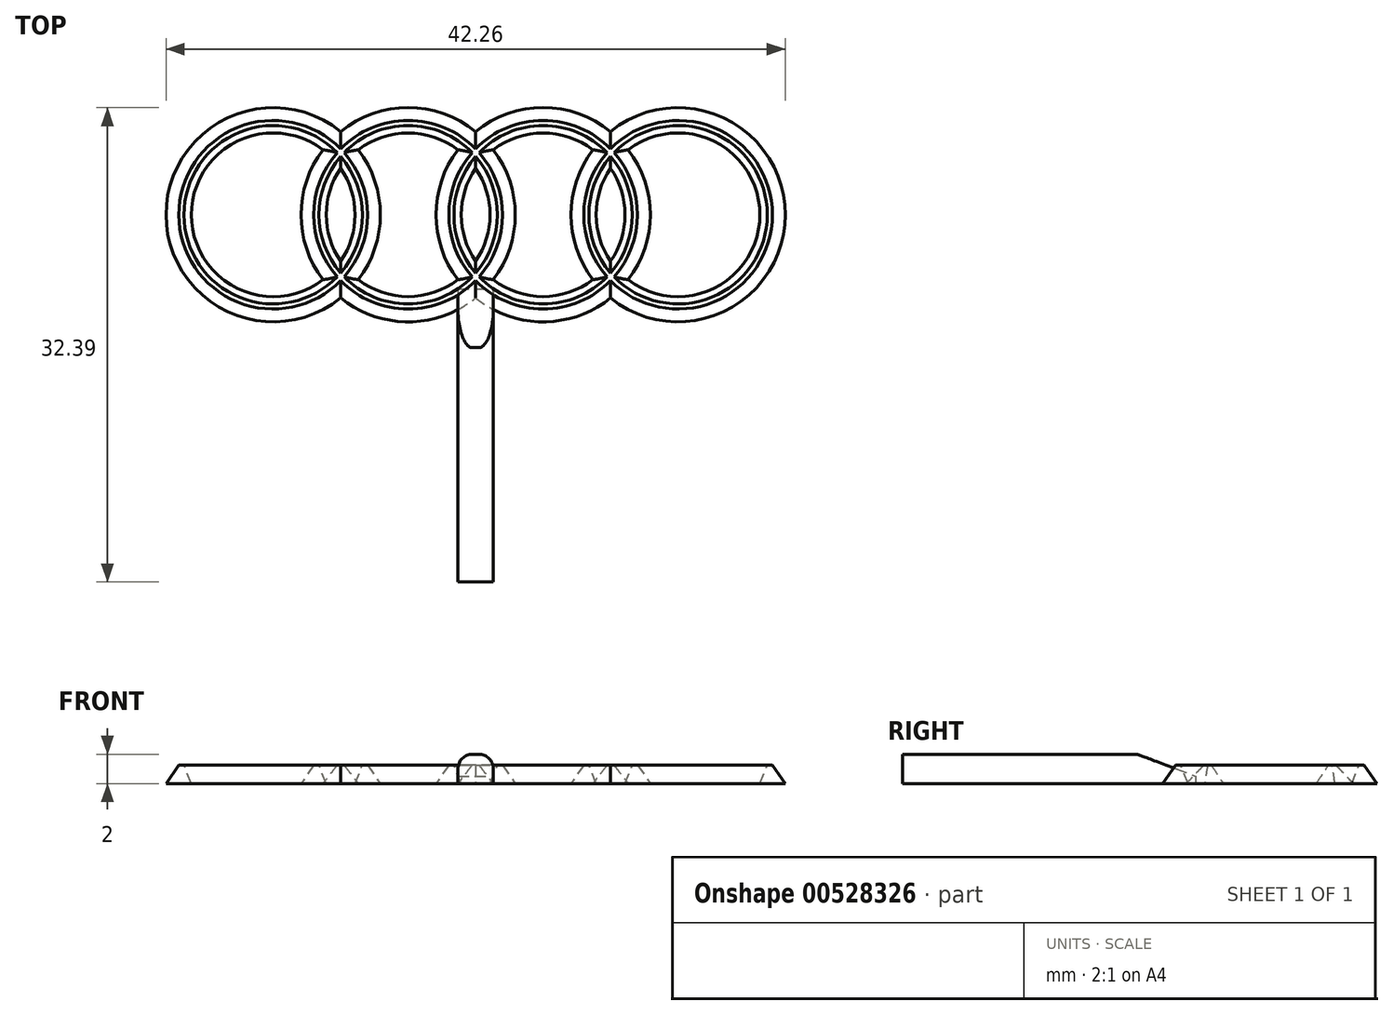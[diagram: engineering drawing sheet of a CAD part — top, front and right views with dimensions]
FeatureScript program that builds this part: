
annotation { "Feature Type Name" : "Feature", "Feature Type Description" : "" }
export const myFeature = defineFeature(function(context is Context, id is Id, definition is map)
    precondition{}
    {
        {
            var Q0;
            Q0=qCreatedBy(makeId("Top.planeOp"),FACE);
            var sketch = newSketch(context, id + "F0", { "sketchPlane" : qUnion([Q0])});
            skLineSegment(sketch, "E0", {"start": v(-55.28, 29.34) * mm, "end": v(-55.28, -29.34) * mm, "construction": true});
            skLineSegment(sketch, "E1", {"start": v(-55.28, -29.34) * mm, "end": v(55.28, -29.34) * mm, "construction": true});
            skLineSegment(sketch, "E2", {"start": v(55.27, -29.34) * mm, "end": v(55.27, 29.34) * mm, "construction": true});
            skLineSegment(sketch, "E3", {"start": v(55.28, 29.34) * mm, "end": v(-67.88, 29.34) * mm, "construction": true});
            skLineSegment(sketch, "E4", {"start": v(-55.28, 0) * mm, "end": v(55.28, 0) * mm, "construction": true});
            skPoint(sketch, "E5", {"position": v(0, 0) * mm});
            skLineSegment(sketch, "E6", {"start": v(-18.43, 29.34) * mm, "end": v(-18.43, -29.34) * mm, "construction": true});
            skLineSegment(sketch, "E7", {"start": v(18.42, -29.34) * mm, "end": v(18.42, 29.34) * mm, "construction": true});
            skCircle(sketch, "E8", {"center": v(-55.28, 0) * mm, "radius": 22.35 * mm});
            skCircle(sketch, "E9", {"center": v(-55.28, 0) * mm, "radius": 29.25 * mm});
            skCircle(sketch, "E10", {"center": v(-18.43, 0) * mm, "radius": 22.35 * mm});
            skCircle(sketch, "E11", {"center": v(-18.43, 0) * mm, "radius": 29.25 * mm});
            skCircle(sketch, "E12", {"center": v(18.42, 0) * mm, "radius": 22.35 * mm});
            skCircle(sketch, "E13", {"center": v(18.42, 0) * mm, "radius": 29.25 * mm});
            skCircle(sketch, "E14", {"center": v(55.28, 0) * mm, "radius": 22.35 * mm});
            skCircle(sketch, "E15", {"center": v(55.28, 0) * mm, "radius": 29.25 * mm});
            skSolve(sketch);
        }
        {
            var Q0;
            {var subQ0=sQuery(id+"F0.wireOp",EDGE,"E12");var subQ1=sQuery(id+"F0.wireOp",EDGE,"E10");var subQ2=makeQuery(id+"F0.imprint","INTERSECT",VERTEX,{"disambiguationData":[OD(0.0)],"derivedFrom":[subQ1,subQ0]});Q0=makeQuery(id+"F0.imprint","IMPRINT",FACE,{"disambiguationData":[TD([[makeQuery(id+"F0.imprint","IMPRINT",EDGE,{"disambiguationData":[TD([[subQ2,1.0]])],"derivedFrom":subQ1}),-1.0]])]});}
            var Q1;
            {var subQ0=sQuery(id+"F0.wireOp",EDGE,"E13");var subQ1=sQuery(id+"F0.wireOp",EDGE,"E10");var subQ2=makeQuery(id+"F0.imprint","INTERSECT",VERTEX,{"disambiguationData":[OD(0.0)],"derivedFrom":[subQ1,subQ0]});Q1=makeQuery(id+"F0.imprint","IMPRINT",FACE,{"disambiguationData":[TD([[makeQuery(id+"F0.imprint","IMPRINT",EDGE,{"disambiguationData":[TD([[subQ2,1.0]])],"derivedFrom":subQ1}),-1.0]])]});}
            var Q2;
            {var subQ0=sQuery(id+"F0.wireOp",EDGE,"E14");var subQ1=sQuery(id+"F0.wireOp",EDGE,"E12");var subQ2=makeQuery(id+"F0.imprint","INTERSECT",VERTEX,{"disambiguationData":[OD(0.0)],"derivedFrom":[subQ1,subQ0]});Q2=makeQuery(id+"F0.imprint","IMPRINT",FACE,{"disambiguationData":[TD([[makeQuery(id+"F0.imprint","IMPRINT",EDGE,{"disambiguationData":[TD([[subQ2,1.0]])],"derivedFrom":subQ1}),-1.0]])]});}
            var Q3;
            {var subQ0=sQuery(id+"F0.wireOp",EDGE,"E15");var subQ1=sQuery(id+"F0.wireOp",EDGE,"E12");var subQ2=makeQuery(id+"F0.imprint","INTERSECT",VERTEX,{"disambiguationData":[OD(0.0)],"derivedFrom":[subQ1,subQ0]});Q3=makeQuery(id+"F0.imprint","IMPRINT",FACE,{"disambiguationData":[TD([[makeQuery(id+"F0.imprint","IMPRINT",EDGE,{"disambiguationData":[TD([[subQ2,1.0]])],"derivedFrom":subQ1}),-1.0]])]});}
            var Q4;
            {var subQ0=sQuery(id+"F0.wireOp",EDGE,"E13");var subQ1=sQuery(id+"F0.wireOp",EDGE,"E10");var subQ2=makeQuery(id+"F0.imprint","INTERSECT",VERTEX,{"disambiguationData":[OD(1.0)],"derivedFrom":[subQ1,subQ0]});Q4=makeQuery(id+"F0.imprint","IMPRINT",FACE,{"disambiguationData":[TD([[makeQuery(id+"F0.imprint","IMPRINT",EDGE,{"disambiguationData":[TD([[subQ2,-1.0]])],"derivedFrom":subQ1}),-1.0]])]});}
            var Q5;
            {var subQ0=sQuery(id+"F0.wireOp",EDGE,"E11");var subQ1=sQuery(id+"F0.wireOp",EDGE,"E8");var subQ2=makeQuery(id+"F0.imprint","INTERSECT",VERTEX,{"disambiguationData":[OD(1.0)],"derivedFrom":[subQ1,subQ0]});Q5=makeQuery(id+"F0.imprint","IMPRINT",FACE,{"disambiguationData":[TD([[makeQuery(id+"F0.imprint","IMPRINT",EDGE,{"disambiguationData":[TD([[subQ2,-1.0]])],"derivedFrom":subQ1}),-1.0]])]});}
            var Q6;
            {var subQ0=sQuery(id+"F0.wireOp",EDGE,"E10");var subQ1=sQuery(id+"F0.wireOp",EDGE,"E8");var subQ2=makeQuery(id+"F0.imprint","INTERSECT",VERTEX,{"disambiguationData":[OD(0.0)],"derivedFrom":[subQ1,subQ0]});Q6=makeQuery(id+"F0.imprint","IMPRINT",FACE,{"disambiguationData":[TD([[makeQuery(id+"F0.imprint","IMPRINT",EDGE,{"disambiguationData":[TD([[subQ2,1.0]])],"derivedFrom":subQ1}),-1.0]])]});}
            var Q7;
            {var subQ0=sQuery(id+"F0.wireOp",EDGE,"E13");var subQ1=sQuery(id+"F0.wireOp",EDGE,"E10");var subQ2=makeQuery(id+"F0.imprint","INTERSECT",VERTEX,{"disambiguationData":[OD(0.0)],"derivedFrom":[subQ1,subQ0]});Q7=makeQuery(id+"F0.imprint","IMPRINT",FACE,{"disambiguationData":[TD([[makeQuery(id+"F0.imprint","IMPRINT",EDGE,{"disambiguationData":[TD([[subQ2,1.0]])],"derivedFrom":subQ1}),1.0]])]});}
            var Q8;
            {var subQ0=sQuery(id+"F0.wireOp",EDGE,"E11");var subQ1=sQuery(id+"F0.wireOp",EDGE,"E8");var subQ2=makeQuery(id+"F0.imprint","INTERSECT",VERTEX,{"disambiguationData":[OD(0.0)],"derivedFrom":[subQ1,subQ0]});Q8=makeQuery(id+"F0.imprint","IMPRINT",FACE,{"disambiguationData":[TD([[makeQuery(id+"F0.imprint","IMPRINT",EDGE,{"disambiguationData":[TD([[subQ2,-1.0]])],"derivedFrom":subQ1}),-1.0]])]});}
            var Q9;
            {var subQ0=sQuery(id+"F0.wireOp",EDGE,"E11");var subQ1=sQuery(id+"F0.wireOp",EDGE,"E9");var subQ2=makeQuery(id+"F0.imprint","INTERSECT",VERTEX,{"disambiguationData":[OD(0.0)],"derivedFrom":[subQ1,subQ0]});Q9=makeQuery(id+"F0.imprint","IMPRINT",FACE,{"disambiguationData":[TD([[makeQuery(id+"F0.imprint","IMPRINT",EDGE,{"disambiguationData":[TD([[subQ2,1.0]])],"derivedFrom":subQ1}),-1.0]])]});}
            var Q10;
            {var subQ0=sQuery(id+"F0.wireOp",EDGE,"E11");var subQ1=sQuery(id+"F0.wireOp",EDGE,"E9");var subQ2=makeQuery(id+"F0.imprint","INTERSECT",VERTEX,{"disambiguationData":[OD(1.0)],"derivedFrom":[subQ1,subQ0]});Q10=makeQuery(id+"F0.imprint","IMPRINT",FACE,{"disambiguationData":[TD([[makeQuery(id+"F0.imprint","IMPRINT",EDGE,{"disambiguationData":[TD([[subQ2,-1.0]])],"derivedFrom":subQ1}),-1.0]])]});}
            var Q11;
            {var subQ0=sQuery(id+"F0.wireOp",EDGE,"E13");var subQ1=sQuery(id+"F0.wireOp",EDGE,"E11");var subQ2=makeQuery(id+"F0.imprint","INTERSECT",VERTEX,{"disambiguationData":[OD(0.0)],"derivedFrom":[subQ1,subQ0]});Q11=makeQuery(id+"F0.imprint","IMPRINT",FACE,{"disambiguationData":[TD([[makeQuery(id+"F0.imprint","IMPRINT",EDGE,{"disambiguationData":[TD([[subQ2,1.0]])],"derivedFrom":subQ1}),-1.0]])]});}
            var Q12;
            {var subQ0=sQuery(id+"F0.wireOp",EDGE,"E13");var subQ1=sQuery(id+"F0.wireOp",EDGE,"E11");var subQ2=makeQuery(id+"F0.imprint","INTERSECT",VERTEX,{"disambiguationData":[OD(1.0)],"derivedFrom":[subQ1,subQ0]});Q12=makeQuery(id+"F0.imprint","IMPRINT",FACE,{"disambiguationData":[TD([[makeQuery(id+"F0.imprint","IMPRINT",EDGE,{"disambiguationData":[TD([[subQ2,-1.0]])],"derivedFrom":subQ1}),-1.0]])]});}
            var Q13;
            {var subQ0=sQuery(id+"F0.wireOp",EDGE,"E15");var subQ1=sQuery(id+"F0.wireOp",EDGE,"E13");var subQ2=makeQuery(id+"F0.imprint","INTERSECT",VERTEX,{"disambiguationData":[OD(0.0)],"derivedFrom":[subQ1,subQ0]});Q13=makeQuery(id+"F0.imprint","IMPRINT",FACE,{"disambiguationData":[TD([[makeQuery(id+"F0.imprint","IMPRINT",EDGE,{"disambiguationData":[TD([[subQ2,1.0]])],"derivedFrom":subQ1}),-1.0]])]});}
            var Q14;
            {var subQ0=sQuery(id+"F0.wireOp",EDGE,"E11");var subQ1=sQuery(id+"F0.wireOp",EDGE,"E8");var subQ2=makeQuery(id+"F0.imprint","INTERSECT",VERTEX,{"disambiguationData":[OD(0.0)],"derivedFrom":[subQ1,subQ0]});Q14=makeQuery(id+"F0.imprint","IMPRINT",FACE,{"disambiguationData":[TD([[makeQuery(id+"F0.imprint","IMPRINT",EDGE,{"disambiguationData":[TD([[subQ2,1.0]])],"derivedFrom":subQ1}),1.0]])]});}
            var Q15;
            {var subQ0=sQuery(id+"F0.wireOp",EDGE,"E11");var subQ1=sQuery(id+"F0.wireOp",EDGE,"E8");var subQ2=makeQuery(id+"F0.imprint","INTERSECT",VERTEX,{"disambiguationData":[OD(0.0)],"derivedFrom":[subQ1,subQ0]});Q15=makeQuery(id+"F0.imprint","IMPRINT",FACE,{"disambiguationData":[TD([[makeQuery(id+"F0.imprint","IMPRINT",EDGE,{"disambiguationData":[TD([[subQ2,1.0]])],"derivedFrom":subQ1}),-1.0]])]});}
            var Q16;
            {var subQ0=sQuery(id+"F0.wireOp",EDGE,"E15");var subQ1=sQuery(id+"F0.wireOp",EDGE,"E12");var subQ2=makeQuery(id+"F0.imprint","INTERSECT",VERTEX,{"disambiguationData":[OD(1.0)],"derivedFrom":[subQ1,subQ0]});Q16=makeQuery(id+"F0.imprint","IMPRINT",FACE,{"disambiguationData":[TD([[makeQuery(id+"F0.imprint","IMPRINT",EDGE,{"disambiguationData":[TD([[subQ2,-1.0]])],"derivedFrom":subQ1}),-1.0]])]});}
            var Q17;
            {var subQ0=sQuery(id+"F0.wireOp",EDGE,"E15");var subQ1=sQuery(id+"F0.wireOp",EDGE,"E12");var subQ2=makeQuery(id+"F0.imprint","INTERSECT",VERTEX,{"disambiguationData":[OD(0.0)],"derivedFrom":[subQ1,subQ0]});Q17=makeQuery(id+"F0.imprint","IMPRINT",FACE,{"disambiguationData":[TD([[makeQuery(id+"F0.imprint","IMPRINT",EDGE,{"disambiguationData":[TD([[subQ2,1.0]])],"derivedFrom":subQ1}),1.0]])]});}
            extrude(context, id + "F1", {"entities" : qUnion([Q0, Q1, Q2, Q3, Q4, Q5, Q6, Q7, Q8, Q9, Q10, Q11, Q12, Q13, Q14, Q15, Q16, Q17]), "depth" : 5 * mm});
        }
        {
            var Q0;
            {var subQ0=sQuery(id+"F0.wireOp",EDGE,"E11");var subQ1=sQuery(id+"F0.wireOp",EDGE,"E9");Q0=makeQuery(id+"F1.opExtrude","CAP_EDGE",EDGE,{"disambiguationData":[OSD([subQ1]),TDD([makeQuery(id+"F0.imprint","IMPRINT",EDGE,{"disambiguationData":[TD([[makeQuery(id+"F0.imprint","INTERSECT",VERTEX,{"disambiguationData":[OD(0.0)],"derivedFrom":[subQ1,subQ0]}),-1.0]])],"derivedFrom":subQ1})])],"isStart":false});}
            var Q1;
            {var subQ0=sQuery(id+"F0.wireOp",EDGE,"E11");Q1=makeQuery(id+"F1.opExtrude","CAP_EDGE",EDGE,{"disambiguationData":[OSD([subQ0]),TDD([makeQuery(id+"F0.imprint","IMPRINT",EDGE,{"disambiguationData":[TD([[makeQuery(id+"F0.imprint","INTERSECT",VERTEX,{"disambiguationData":[OD(0.0)],"derivedFrom":[sQuery(id+"F0.wireOp",EDGE,"E9"),subQ0]}),1.0]])],"derivedFrom":subQ0})])],"isStart":false});}
            var Q2;
            {var subQ0=sQuery(id+"F0.wireOp",EDGE,"E13");Q2=makeQuery(id+"F1.opExtrude","CAP_EDGE",EDGE,{"disambiguationData":[OSD([subQ0]),TDD([makeQuery(id+"F0.imprint","IMPRINT",EDGE,{"disambiguationData":[TD([[makeQuery(id+"F0.imprint","INTERSECT",VERTEX,{"disambiguationData":[OD(0.0)],"derivedFrom":[sQuery(id+"F0.wireOp",EDGE,"E11"),subQ0]}),1.0]])],"derivedFrom":subQ0})])],"isStart":false});}
            var Q3;
            {var subQ0=sQuery(id+"F0.wireOp",EDGE,"E15");var subQ1=sQuery(id+"F0.wireOp",EDGE,"E13");Q3=makeQuery(id+"F1.opExtrude","CAP_EDGE",EDGE,{"disambiguationData":[OSD([subQ0]),TDD([makeQuery(id+"F0.imprint","IMPRINT",EDGE,{"disambiguationData":[TD([[makeQuery(id+"F0.imprint","INTERSECT",VERTEX,{"disambiguationData":[OD(0.0)],"derivedFrom":[subQ1,subQ0]}),1.0]])],"derivedFrom":subQ0})])],"isStart":false});}
            var Q4;
            {var subQ0=sQuery(id+"F0.wireOp",EDGE,"E13");Q4=makeQuery(id+"F1.opExtrude","CAP_EDGE",EDGE,{"disambiguationData":[OSD([subQ0]),TDD([makeQuery(id+"F0.imprint","IMPRINT",EDGE,{"disambiguationData":[TD([[makeQuery(id+"F0.imprint","INTERSECT",VERTEX,{"disambiguationData":[OD(1.0)],"derivedFrom":[sQuery(id+"F0.wireOp",EDGE,"E11"),subQ0]}),-1.0]])],"derivedFrom":subQ0})])],"isStart":false});}
            var Q5;
            {var subQ0=sQuery(id+"F0.wireOp",EDGE,"E11");Q5=makeQuery(id+"F1.opExtrude","CAP_EDGE",EDGE,{"disambiguationData":[OSD([subQ0]),TDD([makeQuery(id+"F0.imprint","IMPRINT",EDGE,{"disambiguationData":[TD([[makeQuery(id+"F0.imprint","INTERSECT",VERTEX,{"disambiguationData":[OD(1.0)],"derivedFrom":[sQuery(id+"F0.wireOp",EDGE,"E9"),subQ0]}),-1.0]])],"derivedFrom":subQ0})])],"isStart":false});}
            var Q6;
            {var subQ0=sQuery(id+"F0.wireOp",EDGE,"E10");var subQ1=sQuery(id+"F0.wireOp",EDGE,"E9");Q6=makeQuery(id+"F1.opExtrude","CAP_EDGE",EDGE,{"disambiguationData":[OSD([subQ1]),TDD([makeQuery(id+"F0.imprint","IMPRINT",EDGE,{"disambiguationData":[TD([[makeQuery(id+"F0.imprint","INTERSECT",VERTEX,{"disambiguationData":[OD(0.0)],"derivedFrom":[subQ1,subQ0]}),1.0]])],"derivedFrom":subQ1})])],"isStart":false});}
            var Q7;
            {var subQ0=sQuery(id+"F0.wireOp",EDGE,"E11");var subQ1=sQuery(id+"F0.wireOp",EDGE,"E8");Q7=makeQuery(id+"F1.opExtrude","CAP_EDGE",EDGE,{"disambiguationData":[OSD([subQ0]),TDD([makeQuery(id+"F0.imprint","IMPRINT",EDGE,{"disambiguationData":[TD([[makeQuery(id+"F0.imprint","INTERSECT",VERTEX,{"disambiguationData":[OD(0.0)],"derivedFrom":[subQ1,subQ0]}),-1.0]])],"derivedFrom":subQ0})])],"isStart":false});}
            var Q8;
            {var subQ0=sQuery(id+"F0.wireOp",EDGE,"E13");var subQ1=sQuery(id+"F0.wireOp",EDGE,"E10");Q8=makeQuery(id+"F1.opExtrude","CAP_EDGE",EDGE,{"disambiguationData":[OSD([subQ0]),TDD([makeQuery(id+"F0.imprint","IMPRINT",EDGE,{"disambiguationData":[TD([[makeQuery(id+"F0.imprint","INTERSECT",VERTEX,{"disambiguationData":[OD(0.0)],"derivedFrom":[subQ1,subQ0]}),-1.0]])],"derivedFrom":subQ0})])],"isStart":false});}
            var Q9;
            {var subQ0=sQuery(id+"F0.wireOp",EDGE,"E12");var subQ1=sQuery(id+"F0.wireOp",EDGE,"E11");Q9=makeQuery(id+"F1.opExtrude","CAP_EDGE",EDGE,{"disambiguationData":[OSD([subQ1]),TDD([makeQuery(id+"F0.imprint","IMPRINT",EDGE,{"disambiguationData":[TD([[makeQuery(id+"F0.imprint","INTERSECT",VERTEX,{"disambiguationData":[OD(0.0)],"derivedFrom":[subQ1,subQ0]}),1.0]])],"derivedFrom":subQ1})])],"isStart":false});}
            var Q10;
            {var subQ0=sQuery(id+"F0.wireOp",EDGE,"E15");var subQ1=sQuery(id+"F0.wireOp",EDGE,"E12");Q10=makeQuery(id+"F1.opExtrude","CAP_EDGE",EDGE,{"disambiguationData":[OSD([subQ0]),TDD([makeQuery(id+"F0.imprint","IMPRINT",EDGE,{"disambiguationData":[TD([[makeQuery(id+"F0.imprint","INTERSECT",VERTEX,{"disambiguationData":[OD(0.0)],"derivedFrom":[subQ1,subQ0]}),-1.0]])],"derivedFrom":subQ0})])],"isStart":false});}
            var Q11;
            {var subQ0=sQuery(id+"F0.wireOp",EDGE,"E14");var subQ1=sQuery(id+"F0.wireOp",EDGE,"E13");Q11=makeQuery(id+"F1.opExtrude","CAP_EDGE",EDGE,{"disambiguationData":[OSD([subQ1]),TDD([makeQuery(id+"F0.imprint","IMPRINT",EDGE,{"disambiguationData":[TD([[makeQuery(id+"F0.imprint","INTERSECT",VERTEX,{"disambiguationData":[OD(0.0)],"derivedFrom":[subQ1,subQ0]}),1.0]])],"derivedFrom":subQ1})])],"isStart":false});}
            chamfer(context, id + "F2", {"entities" : qUnion([Q0, Q1, Q2, Q3, Q4, Q5, Q6, Q7, Q8, Q9, Q10, Q11]), "chamferType" : ChamferType.TWO_OFFSETS, "width1" : 5 * mm, "oppositeDirection" : true, "width2" : 3.5 * mm, "tangentPropagation" : true});
        }
        {
            var Q0;
            {var subQ0=sQuery(id+"F0.wireOp",EDGE,"E11");var subQ1=sQuery(id+"F0.wireOp",EDGE,"E8");Q0=makeQuery(id+"F1.opExtrude","CAP_EDGE",EDGE,{"disambiguationData":[OSD([subQ1]),TDD([makeQuery(id+"F0.imprint","IMPRINT",EDGE,{"disambiguationData":[TD([[makeQuery(id+"F0.imprint","INTERSECT",VERTEX,{"disambiguationData":[OD(0.0)],"derivedFrom":[subQ1,subQ0]}),-1.0]])],"derivedFrom":subQ1})])],"isStart":false});}
            var Q1;
            {var subQ0=sQuery(id+"F0.wireOp",EDGE,"E10");var subQ1=sQuery(id+"F0.wireOp",EDGE,"E8");Q1=makeQuery(id+"F1.opExtrude","CAP_EDGE",EDGE,{"disambiguationData":[OSD([subQ0]),TDD([makeQuery(id+"F0.imprint","IMPRINT",EDGE,{"disambiguationData":[TD([[makeQuery(id+"F0.imprint","INTERSECT",VERTEX,{"disambiguationData":[OD(0.0)],"derivedFrom":[subQ1,subQ0]}),-1.0]])],"derivedFrom":subQ0})])],"isStart":false});}
            var Q2;
            {var subQ0=sQuery(id+"F0.wireOp",EDGE,"E10");var subQ1=sQuery(id+"F0.wireOp",EDGE,"E8");Q2=makeQuery(id+"F1.opExtrude","CAP_EDGE",EDGE,{"disambiguationData":[OSD([subQ1]),TDD([makeQuery(id+"F0.imprint","IMPRINT",EDGE,{"disambiguationData":[TD([[makeQuery(id+"F0.imprint","INTERSECT",VERTEX,{"disambiguationData":[OD(0.0)],"derivedFrom":[subQ1,subQ0]}),1.0]])],"derivedFrom":subQ1})])],"isStart":false});}
            var Q3;
            {var subQ0=sQuery(id+"F0.wireOp",EDGE,"E12");var subQ1=sQuery(id+"F0.wireOp",EDGE,"E10");Q3=makeQuery(id+"F1.opExtrude","CAP_EDGE",EDGE,{"disambiguationData":[OSD([subQ0]),TDD([makeQuery(id+"F0.imprint","IMPRINT",EDGE,{"disambiguationData":[TD([[makeQuery(id+"F0.imprint","INTERSECT",VERTEX,{"disambiguationData":[OD(0.0)],"derivedFrom":[subQ1,subQ0]}),-1.0]])],"derivedFrom":subQ0})])],"isStart":false});}
            var Q4;
            {var subQ0=sQuery(id+"F0.wireOp",EDGE,"E12");var subQ1=sQuery(id+"F0.wireOp",EDGE,"E10");Q4=makeQuery(id+"F1.opExtrude","CAP_EDGE",EDGE,{"disambiguationData":[OSD([subQ1]),TDD([makeQuery(id+"F0.imprint","IMPRINT",EDGE,{"disambiguationData":[TD([[makeQuery(id+"F0.imprint","INTERSECT",VERTEX,{"disambiguationData":[OD(0.0)],"derivedFrom":[subQ1,subQ0]}),1.0]])],"derivedFrom":subQ1})])],"isStart":false});}
            var Q5;
            {var subQ0=sQuery(id+"F0.wireOp",EDGE,"E14");var subQ1=sQuery(id+"F0.wireOp",EDGE,"E12");Q5=makeQuery(id+"F1.opExtrude","CAP_EDGE",EDGE,{"disambiguationData":[OSD([subQ0]),TDD([makeQuery(id+"F0.imprint","IMPRINT",EDGE,{"disambiguationData":[TD([[makeQuery(id+"F0.imprint","INTERSECT",VERTEX,{"disambiguationData":[OD(0.0)],"derivedFrom":[subQ1,subQ0]}),-1.0]])],"derivedFrom":subQ0})])],"isStart":false});}
            var Q6;
            {var subQ0=sQuery(id+"F0.wireOp",EDGE,"E14");var subQ1=sQuery(id+"F0.wireOp",EDGE,"E12");Q6=makeQuery(id+"F1.opExtrude","CAP_EDGE",EDGE,{"disambiguationData":[OSD([subQ1]),TDD([makeQuery(id+"F0.imprint","IMPRINT",EDGE,{"disambiguationData":[TD([[makeQuery(id+"F0.imprint","INTERSECT",VERTEX,{"disambiguationData":[OD(0.0)],"derivedFrom":[subQ1,subQ0]}),1.0]])],"derivedFrom":subQ1})])],"isStart":false});}
            var Q7;
            {var subQ0=sQuery(id+"F0.wireOp",EDGE,"E12");Q7=makeQuery(id+"F1.opExtrude","CAP_EDGE",EDGE,{"disambiguationData":[OSD([subQ0]),TDD([makeQuery(id+"F0.imprint","IMPRINT",EDGE,{"disambiguationData":[TD([[makeQuery(id+"F0.imprint","INTERSECT",VERTEX,{"disambiguationData":[OD(0.0)],"derivedFrom":[sQuery(id+"F0.wireOp",EDGE,"E11"),subQ0]}),1.0]])],"derivedFrom":subQ0})])],"isStart":false});}
            var Q8;
            {var subQ0=sQuery(id+"F0.wireOp",EDGE,"E10");Q8=makeQuery(id+"F1.opExtrude","CAP_EDGE",EDGE,{"disambiguationData":[OSD([subQ0]),TDD([makeQuery(id+"F0.imprint","IMPRINT",EDGE,{"disambiguationData":[TD([[makeQuery(id+"F0.imprint","INTERSECT",VERTEX,{"disambiguationData":[OD(0.0)],"derivedFrom":[sQuery(id+"F0.wireOp",EDGE,"E9"),subQ0]}),1.0]])],"derivedFrom":subQ0})])],"isStart":false});}
            var Q9;
            {var subQ0=sQuery(id+"F0.wireOp",EDGE,"E10");Q9=makeQuery(id+"F1.opExtrude","CAP_EDGE",EDGE,{"disambiguationData":[OSD([subQ0]),TDD([makeQuery(id+"F0.imprint","IMPRINT",EDGE,{"disambiguationData":[TD([[makeQuery(id+"F0.imprint","INTERSECT",VERTEX,{"disambiguationData":[OD(1.0)],"derivedFrom":[sQuery(id+"F0.wireOp",EDGE,"E9"),subQ0]}),-1.0]])],"derivedFrom":subQ0})])],"isStart":false});}
            var Q10;
            {var subQ0=sQuery(id+"F0.wireOp",EDGE,"E12");Q10=makeQuery(id+"F1.opExtrude","CAP_EDGE",EDGE,{"disambiguationData":[OSD([subQ0]),TDD([makeQuery(id+"F0.imprint","IMPRINT",EDGE,{"disambiguationData":[TD([[makeQuery(id+"F0.imprint","INTERSECT",VERTEX,{"disambiguationData":[OD(1.0)],"derivedFrom":[sQuery(id+"F0.wireOp",EDGE,"E11"),subQ0]}),-1.0]])],"derivedFrom":subQ0})])],"isStart":false});}
            var Q11;
            {var subQ0=sQuery(id+"F0.wireOp",EDGE,"E14");var subQ1=sQuery(id+"F0.wireOp",EDGE,"E13");Q11=makeQuery(id+"F1.opExtrude","CAP_EDGE",EDGE,{"disambiguationData":[OSD([subQ0]),TDD([makeQuery(id+"F0.imprint","IMPRINT",EDGE,{"disambiguationData":[TD([[makeQuery(id+"F0.imprint","INTERSECT",VERTEX,{"disambiguationData":[OD(0.0)],"derivedFrom":[subQ1,subQ0]}),1.0]])],"derivedFrom":subQ0})])],"isStart":false});}
            chamfer(context, id + "F3", {"entities" : qUnion([Q0, Q1, Q2, Q3, Q4, Q5, Q6, Q7, Q8, Q9, Q10, Q11]), "chamferType" : ChamferType.TWO_OFFSETS, "width1" : 5 * mm, "oppositeDirection" : false, "width2" : 2 * mm, "tangentPropagation" : true});
        }
        {
            var Q0;
            Q0=makeQuery(id+"F1.opExtrude","SWEPT_BODY",BODY,{"disambiguationData":[OSD([sQuery(id+"F0.wireOp",EDGE,"E8"),sQuery(id+"F0.wireOp",EDGE,"E9"),sQuery(id+"F0.wireOp",EDGE,"E10"),sQuery(id+"F0.wireOp",EDGE,"E11"),sQuery(id+"F0.wireOp",EDGE,"E12"),sQuery(id+"F0.wireOp",EDGE,"E13"),sQuery(id+"F0.wireOp",EDGE,"E14"),sQuery(id+"F0.wireOp",EDGE,"E15")])]});
            var Q1;
            Q1=qCreatedBy(makeId("Origin.pointOp"),VERTEX);
            transform(context, id + "F4", {"entities" : qUnion([Q0]), "transformType" : TransformType.SCALE_UNIFORMLY, "scale" : 0.25, "scalePoint" : qUnion([Q1]), "makeCopy" : false});
        }
        {
            var Q0;
            Q0=qCreatedBy(makeId("Top.planeOp"),FACE);
            var sketch = newSketch(context, id + "F5", { "sketchPlane" : qUnion([Q0])});
            skArc(sketch, "E16.0", {"start": v(-9.21, 5.68) * mm, "mid": v(-21.13, 0) * mm, "end": v(-9.21, -5.68) * mm, "construction": true});
            skArc(sketch, "E17.0", {"start": v(9.21, -5.68) * mm, "mid": v(21.13, 0) * mm, "end": v(9.21, 5.68) * mm, "construction": true});
            skArc(sketch, "E18.0", {"start": v(0, -5.68) * mm, "mid": v(4.6, -7.31) * mm, "end": v(9.21, -5.68) * mm, "construction": true});
            skArc(sketch, "E19.0", {"start": v(-9.21, -5.68) * mm, "mid": v(-4.6, -7.31) * mm, "end": v(0, -5.68) * mm, "construction": true});
            skArc(sketch, "E20.0", {"start": v(0, 5.68) * mm, "mid": v(-4.6, 7.31) * mm, "end": v(-9.21, 5.68) * mm, "construction": true});
            skArc(sketch, "E21.0", {"start": v(9.21, 5.68) * mm, "mid": v(4.6, 7.31) * mm, "end": v(0, 5.68) * mm, "construction": true});
            skLineSegment(sketch, "E22", {"start": v(-21.13, 0) * mm, "end": v(21.13, 0) * mm, "construction": true});
            skPoint(sketch, "E22.startSnap0", {"position": v(-21.13, 0) * mm});
            skLineSegment(sketch, "E23.bottom", {"start": v(-51.13, 0.8) * mm, "end": v(-21.13, 0.8) * mm});
            skLineSegment(sketch, "E23.top", {"start": v(-51.13, -0.8) * mm, "end": v(-21.13, -0.8) * mm});
            skLineSegment(sketch, "E23.left", {"start": v(-51.13, 0.8) * mm, "end": v(-51.13, -0.8) * mm});
            skLineSegment(sketch, "E23.right", {"start": v(-21.13, 0.8) * mm, "end": v(-21.13, -0.8) * mm});
            skPoint(sketch, "E24.orphan", {"position": v(-32.97, 0) * mm});
            skLineSegment(sketch, "E25.bottom", {"start": v(21.13, -0.8) * mm, "end": v(51.13, -0.8) * mm});
            skLineSegment(sketch, "E25.top", {"start": v(21.13, 0.8) * mm, "end": v(51.13, 0.8) * mm});
            skLineSegment(sketch, "E25.left", {"start": v(21.13, -0.8) * mm, "end": v(21.13, 0.8) * mm});
            skLineSegment(sketch, "E25.right", {"start": v(51.13, -0.8) * mm, "end": v(51.13, 0.8) * mm});
            skPoint(sketch, "E26", {"position": v(21.13, 0) * mm});
            skLineSegment(sketch, "E27", {"start": v(-23.13, -0.8) * mm, "end": v(-23.13, 0.8) * mm});
            skLineSegment(sketch, "E28", {"start": v(23.13, -0.8) * mm, "end": v(23.13, 0.8) * mm});
            skLineSegment(sketch, "E29.bottom", {"start": v(-21.13, -0.8) * mm, "end": v(-20.13, -0.8) * mm});
            skLineSegment(sketch, "E29.top", {"start": v(-21.13, 0.8) * mm, "end": v(-20.13, 0.8) * mm});
            skLineSegment(sketch, "E29.left", {"start": v(-21.13, -0.8) * mm, "end": v(-21.13, 0.8) * mm});
            skLineSegment(sketch, "E29.right", {"start": v(-20.13, -0.8) * mm, "end": v(-20.13, 0.8) * mm});
            skLineSegment(sketch, "E30.bottom", {"start": v(21.13, -0.8) * mm, "end": v(20.13, -0.8) * mm});
            skLineSegment(sketch, "E30.top", {"start": v(21.13, 0.8) * mm, "end": v(20.13, 0.8) * mm});
            skLineSegment(sketch, "E30.right", {"start": v(20.13, -0.8) * mm, "end": v(20.13, 0.8) * mm});
            skSolve(sketch);
        }
        {
            var Q0;
            Q0=makeQuery(id+"F1.opExtrude","CAP_FACE",FACE,{"disambiguationData":[OSD([sQuery(id+"F0.wireOp",EDGE,"E8"),sQuery(id+"F0.wireOp",EDGE,"E9"),sQuery(id+"F0.wireOp",EDGE,"E10"),sQuery(id+"F0.wireOp",EDGE,"E11"),sQuery(id+"F0.wireOp",EDGE,"E12"),sQuery(id+"F0.wireOp",EDGE,"E13"),sQuery(id+"F0.wireOp",EDGE,"E14"),sQuery(id+"F0.wireOp",EDGE,"E15")])],"isStart":true});
            var sketch = newSketch(context, id + "F6", { "sketchPlane" : qUnion([Q0])});
            skLineSegment(sketch, "E31.bottom", {"start": v(1.2, 5.08) * mm, "end": v(-1.2, 5.08) * mm});
            skLineSegment(sketch, "E31.top", {"start": v(1.2, 25.08) * mm, "end": v(-1.2, 25.08) * mm});
            skLineSegment(sketch, "E31.left", {"start": v(1.2, 5.08) * mm, "end": v(1.2, 25.08) * mm});
            skLineSegment(sketch, "E31.right", {"start": v(-1.2, 5.08) * mm, "end": v(-1.2, 25.08) * mm});
            skSolve(sketch);
        }
        {
            var Q0;
            {var subQ11=sQuery(id+"F6.wireOp",EDGE,"E31.top");Q0=makeQuery(id+"F6.imprint","IMPRINT",FACE,{"disambiguationData":[TD([[makeQuery(id+"F6.imprint","IMPRINT",EDGE,{"derivedFrom":subQ11}),1.0]])]});}
            var Q1;
            {var subQ13=sQuery(id+"F6.wireOp",EDGE,"E31.bottom");Q1=makeQuery(id+"F6.imprint","IMPRINT",FACE,{"disambiguationData":[TD([[makeQuery(id+"F6.imprint","IMPRINT",EDGE,{"derivedFrom":subQ13}),-1.0]])]});}
            extrude(context, id + "F7", {"entities" : qUnion([Q0, Q1]), "oppositeDirection" : true, "depth" : 2 * mm, "offsetDistance" : 25 * mm});
        }
        {
            var Q0;
            Q0=makeQuery(id+"F7.opExtrude","CAP_EDGE",EDGE,{"disambiguationData":[OSD([sQuery(id+"F6.wireOp",EDGE,"E31.bottom")])],"isStart":false});
            chamfer(context, id + "F8", {"entities" : qUnion([Q0]), "chamferType" : ChamferType.TWO_OFFSETS, "width1" : 4 * mm, "oppositeDirection" : false, "width2" : 1.5 * mm, "tangentPropagation" : true});
        }
        {
            var Q0;
            Q0=makeQuery(id+"F7.opExtrude","CAP_EDGE",EDGE,{"disambiguationData":[OSD([sQuery(id+"F6.wireOp",EDGE,"E31.right")])],"isStart":false});
            var Q1;
            Q1=makeQuery(id+"F7.opExtrude","CAP_EDGE",EDGE,{"disambiguationData":[OSD([sQuery(id+"F6.wireOp",EDGE,"E31.left")])],"isStart":false});
            fillet(context, id + "F9", {"entities" : qUnion([Q0, Q1]), "radius" : 1 * mm, "tangentPropagation" : true, "allowEdgeOverflow" : false});
        }
    });
